# Revit family: pc-rp40160kal20_50hz
name_source: partatom
category: 機械設備
units: mm (PartAtom-declared; Revit-internal decimal feet)

## family parameters
OmniClass タイトル = Split System Air Conditioning Units
OmniClass 番号 = 23.75.10.24.21.27.27
パーツ タイプ = 標準
ロード時にボイドで切り取り = いいえ
丸型コネクタ寸法 = 直径を使用
作業面ベース = いいえ
共有 = いいえ
常に垂直 = はい
部屋計算ポイント = はい

## types (20) — shared parameters
Clearance Bottom = 1800  [stored 5.90551 ft]
Clearance Front = 1500  [stored 4.92126 ft]
Clearance Left = 270  [stored 0.885827 ft]
Clearance Right = 300  [stored 0.984252 ft]
Clearance Top = 1  [stored 0.00328084 ft]
Depth = 680  [stored 2.23097 ft]
Height = 236
Height_本体 = 230  [stored 0.754593 ft]
IfcExportAs = IfcUnitaryEquipmentType
IfcExportType = AIRCONDITIONINGUNIT
OmniClassCode = 23-33 17 13 11
URL = https://www.mitsubishielectric.co.jp
Uniclass2015Code = Pr_70_65_03_84
Uniclass2015Title = Split coil remote air cooled condensing units
Uniclass2015Version = Systems v1.9
ケーブルサイズ1 = 0 mm
サービススペース = はい
ドレン管径 = 20 mm
ドレン管径 (外径) = 26 mm
ドレン管高さ = 190  [stored 0.62336 ft]
パネルマテリアル = <カテゴリ別>
仕様書バージョン = Version1.0
企業コード = 108420
冷媒ガス管高さ = 126  [stored 0.413386 ft]
冷媒液管高さ = 126  [stored 0.413386 ft]
冷媒管径 = 100 mm
冷媒高低圧ガス管径 = 0 mm
分類コード = 5.0053E+13
加湿給水管径 = 0 mm
参照している仕様書等のバージョン = 公共建築物標準仕様書（機械設備工事編）平成31年度版
吊りボルト_H = 50  [stored 0.164042 ft]
吊り位置Y = 320  [stored 1.04987 ft]
周波数 = 50 Hz
呼称 = 室内機_天井吊(露出)形
始動方式 = 直入
形式 = 天井吊（露出）形
推奨ブレーカー容量 = 0 A
本体マテリアル = <カテゴリ別>
極数 = 1
法定耐用年数 = 6
点検口 = はい
発停方法 = 付属スイッチ
相 = 1
積算_科目 = 1 空気調和設備
符号 = ACP-CR
背面_ドレン管接続口 = 233  [stored 0.764436 ft]
製品出荷対象 = 国内
製造元 = 三菱電機株式会社
設置方法 = 天井吊形
設計冷房能力 = 0 kW
設計冷房能力_顕熱 = 0 kW
設計暖房能力 = 0.00 kW
説明 = 店舗・事務所用パッケージエアコン(Mr.SLIM) [本体] 天吊形室内機
負荷分類 = 3_ファン類
運転質量 = 0.00 kg
電圧 = 0 V
zero-valued in all types: Clearance Back, 価格, 有効加湿量, 点検口設置範囲, 電源_H

## per-type parameters (varying)
- 天吊_PC-RP45KAL20: MAX風量=780.0 m³/h; MID風量=660.0 m³/h; MID風量2=600.0 m³/h; MIN風量=540.0 m³/h; Width=960  [stored 3.14961 ft]; モデル=PC-RP45KAL20; 冷媒ガス管径=13 mm; 冷媒液管径=6 mm; 冷媒管径符号=Ac; 冷房能力=4 kW; 吊り位置X=917  [stored 3.00853 ft]; 暖房能力=4.50 kW; 消費電力=0.05 kW; 消費電力_冷房=0.05 kW; 消費電力_暖房=0.04 kW; 背面_ガス管接続口=203  [stored 0.66601 ft]; 背面_液管接続口=184  [stored 0.603675 ft]; 製品質量=24.00 kg; 質量=28.80 kg; 電動機出力_送風機=0.09 kW; 音響パワーレベル(dB)=55; 音響パワーレベル_中 (dB)=53; 音響パワーレベル_弱 (dB)=50; 音響パワーレベル_強 (dB)=55; 音響パワーレベル_静 (dB)=48; 風量=780.0 m³/h; 風量_中 (㎥/min)=11; 風量_弱 (㎥/min)=10; 風量_強 (㎥/min)=13; 風量_静 (㎥/min)=9
- 天吊_PC-RP56KAL20: MAX風量=780.0 m³/h; MID風量=720.0 m³/h; MID風量2=660.0 m³/h; MIN風量=600.0 m³/h; Width=960  [stored 3.14961 ft]; モデル=PC-RP56KAL20; 冷媒ガス管径=13 mm; 冷媒液管径=6 mm; 冷媒管径符号=Ac; 冷房能力=5 kW; 吊り位置X=917  [stored 3.00853 ft]; 暖房能力=5.60 kW; 消費電力=0.06 kW; 消費電力_冷房=0.06 kW; 消費電力_暖房=0.05 kW; 背面_ガス管接続口=203  [stored 0.66601 ft]; 背面_液管接続口=184  [stored 0.603675 ft]; 製品質量=25.00 kg; 質量=30.00 kg; 電動機出力_送風機=0.09 kW; 音響パワーレベル(dB)=55; 音響パワーレベル_中 (dB)=53; 音響パワーレベル_弱 (dB)=50; 音響パワーレベル_強 (dB)=55; 音響パワーレベル_静 (dB)=48; 風量=780.0 m³/h; 風量_中 (㎥/min)=12; 風量_弱 (㎥/min)=11; 風量_強 (㎥/min)=13; 風量_静 (㎥/min)=10
- 天吊_PC-RP71KAL20: MAX風量=1200.0 m³/h; MID風量=1080.0 m³/h; MID風量2=960.0 m³/h; MIN風量=780.0 m³/h; Width=1280  [stored 4.19948 ft]; モデル=PC-RP71KAL20; 冷媒ガス管径=16 mm; 冷媒液管径=10 mm; 冷媒管径符号=Bd; 冷房能力=6.3 kW; 吊り位置X=1237  [stored 4.0584 ft]; 暖房能力=7.10 kW; 消費電力=0.10 kW; 消費電力_冷房=0.10 kW; 消費電力_暖房=0.09 kW; 背面_ガス管接続口=200  [stored 0.656168 ft]; 背面_液管接続口=180  [stored 0.590551 ft]; 製品質量=32.00 kg; 質量=38.40 kg; 電動機出力_送風機=0.10 kW; 音響パワーレベル(dB)=57; 音響パワーレベル_中 (dB)=55; 音響パワーレベル_弱 (dB)=53; 音響パワーレベル_強 (dB)=57; 音響パワーレベル_静 (dB)=50; 風量=1200.0 m³/h; 風量_中 (㎥/min)=18; 風量_弱 (㎥/min)=16; 風量_強 (㎥/min)=20; 風量_静 (㎥/min)=13
- 天吊_PC-RP80KAL20: MAX風量=1200.0 m³/h; MID風量=1080.0 m³/h; MID風量2=960.0 m³/h; MIN風量=780.0 m³/h; Width=1280  [stored 4.19948 ft]; モデル=PC-RP80KAL20; 冷媒ガス管径=16 mm; 冷媒液管径=10 mm; 冷媒管径符号=Bd; 冷房能力=7.1 kW; 吊り位置X=1237  [stored 4.0584 ft]; 暖房能力=8.00 kW; 消費電力=0.10 kW; 消費電力_冷房=0.10 kW; 消費電力_暖房=0.09 kW; 背面_ガス管接続口=200  [stored 0.656168 ft]; 背面_液管接続口=180  [stored 0.590551 ft]; 製品質量=32.00 kg; 質量=38.40 kg; 電動機出力_送風機=0.10 kW; 音響パワーレベル(dB)=57; 音響パワーレベル_中 (dB)=55; 音響パワーレベル_弱 (dB)=53; 音響パワーレベル_強 (dB)=57; 音響パワーレベル_静 (dB)=50; 風量=1200.0 m³/h; 風量_中 (㎥/min)=18; 風量_弱 (㎥/min)=16; 風量_強 (㎥/min)=20; 風量_静 (㎥/min)=13
- 天吊_PC-RP112KAL20: MAX風量=1740.0 m³/h; MID風量=1560.0 m³/h; MID風量2=1320.0 m³/h; MIN風量=1200.0 m³/h; Width=1600  [stored 5.24934 ft]; モデル=PC-RP112KAL20; 冷媒ガス管径=16 mm; 冷媒液管径=10 mm; 冷媒管径符号=Bd; 冷房能力=10 kW; 吊り位置X=1557  [stored 5.10827 ft]; 暖房能力=11.20 kW; 消費電力=0.12 kW; 消費電力_冷房=0.12 kW; 消費電力_暖房=0.11 kW; 背面_ガス管接続口=200  [stored 0.656168 ft]; 背面_液管接続口=180  [stored 0.590551 ft]; 製品質量=38.00 kg; 質量=45.60 kg; 電動機出力_送風機=0.16 kW; 音響パワーレベル(dB)=62; 音響パワーレベル_中 (dB)=59; 音響パワーレベル_弱 (dB)=56; 音響パワーレベル_強 (dB)=62; 音響パワーレベル_静 (dB)=54; 風量=1740.0 m³/h; 風量_中 (㎥/min)=26; 風量_弱 (㎥/min)=22; 風量_強 (㎥/min)=29; 風量_静 (㎥/min)=20
- 天吊_PC-RP140KAL20: MAX風量=1860.0 m³/h; MID風量=1620.0 m³/h; MID風量2=1440.0 m³/h; MIN風量=1260.0 m³/h; Width=1600  [stored 5.24934 ft]; モデル=PC-RP140KAL20; 冷媒ガス管径=16 mm; 冷媒液管径=10 mm; 冷媒管径符号=Bd; 冷房能力=12.5 kW; 吊り位置X=1557  [stored 5.10827 ft]; 暖房能力=14.00 kW; 消費電力=0.14 kW; 消費電力_冷房=0.14 kW; 消費電力_暖房=0.13 kW; 背面_ガス管接続口=200  [stored 0.656168 ft]; 背面_液管接続口=180  [stored 0.590551 ft]; 製品リリース年月=0; 製品質量=38.00 kg; 質量=45.60 kg; 電動機出力_送風機=0.16 kW; 音響パワーレベル(dB)=63; 音響パワーレベル_中 (dB)=61; 音響パワーレベル_弱 (dB)=58; 音響パワーレベル_強 (dB)=63; 音響パワーレベル_静 (dB)=56; 風量=1860.0 m³/h; 風量_中 (㎥/min)=27; 風量_弱 (㎥/min)=24; 風量_強 (㎥/min)=31; 風量_静 (㎥/min)=21
- 天吊_PC-RP160KAL20: MAX風量=1980.0 m³/h; MID風量=1680.0 m³/h; MID風量2=1500.0 m³/h; MIN風量=1320.0 m³/h; Width=1600  [stored 5.24934 ft]; モデル=PC-RP160KAL20; 冷媒ガス管径=16 mm; 冷媒液管径=10 mm; 冷媒管径符号=Bd; 冷房能力=14 kW; 吊り位置X=1557  [stored 5.10827 ft]; 暖房能力=16.00 kW; 消費電力=0.17 kW; 消費電力_冷房=0.17 kW; 消費電力_暖房=0.16 kW; 背面_ガス管接続口=200  [stored 0.656168 ft]; 背面_液管接続口=180  [stored 0.590551 ft]; 製品質量=38.00 kg; 質量=45.60 kg; 電動機出力_送風機=0.16 kW; 音響パワーレベル(dB)=65; 音響パワーレベル_中 (dB)=62; 音響パワーレベル_弱 (dB)=60; 音響パワーレベル_強 (dB)=65; 音響パワーレベル_静 (dB)=58; 風量=1980.0 m³/h; 風量_中 (㎥/min)=28; 風量_弱 (㎥/min)=25; 風量_強 (㎥/min)=33; 風量_静 (㎥/min)=22
- 天吊_PC-RP63KAL20: MAX風量=1020.0 m³/h; MID風量=900.0 m³/h; MID風量2=840.0 m³/h; MIN風量=720.0 m³/h; Width=1280  [stored 4.19948 ft]; モデル=PC-RP63KAL20; 冷媒ガス管径=13 mm; 冷媒液管径=6 mm; 冷媒管径符号=Ac; 冷房能力=5.6 kW; 吊り位置X=1237  [stored 4.0584 ft]; 暖房能力=6.30 kW; 消費電力=0.07 kW; 消費電力_冷房=0.07 kW; 消費電力_暖房=0.06 kW; 背面_ガス管接続口=203  [stored 0.66601 ft]; 背面_液管接続口=184  [stored 0.603675 ft]; 製品質量=32.00 kg; 質量=38.40 kg; 電動機出力_送風機=0.10 kW; 音響パワーレベル(dB)=55; 音響パワーレベル_中 (dB)=53; 音響パワーレベル_弱 (dB)=51; 音響パワーレベル_強 (dB)=55; 音響パワーレベル_静 (dB)=49; 風量=1020.0 m³/h; 風量_中 (㎥/min)=15; 風量_弱 (㎥/min)=14; 風量_強 (㎥/min)=17; 風量_静 (㎥/min)=12
- 天吊_PC-RP40KAL20: MAX風量=780.0 m³/h; MID風量=660.0 m³/h; MID風量2=600.0 m³/h; MIN風量=540.0 m³/h; Width=960  [stored 3.14961 ft]; モデル=PC-RP40KAL20; 冷媒ガス管径=13 mm; 冷媒液管径=6 mm; 冷媒管径符号=Ac; 冷房能力=3.6 kW; 吊り位置X=917  [stored 3.00853 ft]; 暖房能力=4.00 kW; 消費電力=0.05 kW; 消費電力_冷房=0.05 kW; 消費電力_暖房=0.04 kW; 背面_ガス管接続口=203  [stored 0.66601 ft]; 背面_液管接続口=184  [stored 0.603675 ft]; 製品質量=24.00 kg; 質量=28.80 kg; 電動機出力_送風機=0.09 kW; 音響パワーレベル(dB)=55; 音響パワーレベル_中 (dB)=53; 音響パワーレベル_弱 (dB)=50; 音響パワーレベル_強 (dB)=55; 音響パワーレベル_静 (dB)=48; 風量=780.0 m³/h; 風量_中 (㎥/min)=11; 風量_弱 (㎥/min)=10; 風量_強 (㎥/min)=13; 風量_静 (㎥/min)=9
- 天吊_PC-RP50KAL20: MAX風量=780.0 m³/h; MID風量=720.0 m³/h; MID風量2=660.0 m³/h; MIN風量=600.0 m³/h; Width=960  [stored 3.14961 ft]; モデル=PC-RP50KAL20; 冷媒ガス管径=13 mm; 冷媒液管径=6 mm; 冷媒管径符号=Ac; 冷房能力=4.5 kW; 吊り位置X=917  [stored 3.00853 ft]; 暖房能力=5.00 kW; 消費電力=0.06 kW; 消費電力_冷房=0.06 kW; 消費電力_暖房=0.05 kW; 背面_ガス管接続口=203  [stored 0.66601 ft]; 背面_液管接続口=184  [stored 0.603675 ft]; 製品質量=25.00 kg; 質量=30.00 kg; 電動機出力_送風機=0.09 kW; 音響パワーレベル(dB)=55; 音響パワーレベル_中 (dB)=53; 音響パワーレベル_弱 (dB)=50; 音響パワーレベル_強 (dB)=55; 音響パワーレベル_静 (dB)=48; 風量=780.0 m³/h; 風量_中 (㎥/min)=12; 風量_弱 (㎥/min)=11; 風量_強 (㎥/min)=13; 風量_静 (㎥/min)=10
- 天吊_PC-RP112KA20: MAX風量=1740.0 m³/h; MID風量=1560.0 m³/h; MID風量2=1320.0 m³/h; MIN風量=1200.0 m³/h; Width=1600  [stored 5.24934 ft]; モデル=PC-RP112KA20; 冷媒ガス管径=16 mm; 冷媒液管径=10 mm; 冷媒管径符号=Bd; 冷房能力=10 kW; 吊り位置X=1557  [stored 5.10827 ft]; 暖房能力=11.20 kW; 消費電力=0.12 kW; 消費電力_冷房=0.12 kW; 消費電力_暖房=0.11 kW; 背面_ガス管接続口=200  [stored 0.656168 ft]; 背面_液管接続口=180  [stored 0.590551 ft]; 製品質量=38.00 kg; 質量=45.60 kg; 電動機出力_送風機=0.16 kW; 音響パワーレベル(dB)=62; 音響パワーレベル_中 (dB)=59; 音響パワーレベル_弱 (dB)=56; 音響パワーレベル_強 (dB)=62; 音響パワーレベル_静 (dB)=54; 風量=1740.0 m³/h; 風量_中 (㎥/min)=26; 風量_弱 (㎥/min)=22; 風量_強 (㎥/min)=29; 風量_静 (㎥/min)=20
- 天吊_PC-RP140KA20: MAX風量=1860.0 m³/h; MID風量=1620.0 m³/h; MID風量2=1440.0 m³/h; MIN風量=1260.0 m³/h; Width=1600  [stored 5.24934 ft]; モデル=PC-RP140KA20; 冷媒ガス管径=16 mm; 冷媒液管径=10 mm; 冷媒管径符号=Bd; 冷房能力=12.5 kW; 吊り位置X=1557  [stored 5.10827 ft]; 暖房能力=14.00 kW; 消費電力=0.14 kW; 消費電力_冷房=0.14 kW; 消費電力_暖房=0.13 kW; 背面_ガス管接続口=200  [stored 0.656168 ft]; 背面_液管接続口=180  [stored 0.590551 ft]; 製品質量=38.00 kg; 質量=45.60 kg; 電動機出力_送風機=0.16 kW; 音響パワーレベル(dB)=63; 音響パワーレベル_中 (dB)=61; 音響パワーレベル_弱 (dB)=58; 音響パワーレベル_強 (dB)=63; 音響パワーレベル_静 (dB)=56; 風量=1860.0 m³/h; 風量_中 (㎥/min)=27; 風量_弱 (㎥/min)=24; 風量_強 (㎥/min)=31; 風量_静 (㎥/min)=21
- 天吊_PC-RP160KA20: MAX風量=1980.0 m³/h; MID風量=1680.0 m³/h; MID風量2=1500.0 m³/h; MIN風量=1320.0 m³/h; Width=1600  [stored 5.24934 ft]; モデル=PC-RP160KA20; 冷媒ガス管径=16 mm; 冷媒液管径=10 mm; 冷媒管径符号=Bd; 冷房能力=14 kW; 吊り位置X=1557  [stored 5.10827 ft]; 暖房能力=16.00 kW; 消費電力=0.17 kW; 消費電力_冷房=0.17 kW; 消費電力_暖房=0.16 kW; 背面_ガス管接続口=200  [stored 0.656168 ft]; 背面_液管接続口=180  [stored 0.590551 ft]; 製品質量=38.00 kg; 質量=45.60 kg; 電動機出力_送風機=0.16 kW; 音響パワーレベル(dB)=65; 音響パワーレベル_中 (dB)=62; 音響パワーレベル_弱 (dB)=60; 音響パワーレベル_強 (dB)=65; 音響パワーレベル_静 (dB)=58; 風量=1980.0 m³/h; 風量_中 (㎥/min)=28; 風量_弱 (㎥/min)=25; 風量_強 (㎥/min)=33; 風量_静 (㎥/min)=22
- 天吊_PC-RP40KA20: MAX風量=780.0 m³/h; MID風量=660.0 m³/h; MID風量2=600.0 m³/h; MIN風量=540.0 m³/h; Width=960  [stored 3.14961 ft]; モデル=PC-RP40KA20; 冷媒ガス管径=13 mm; 冷媒液管径=6 mm; 冷媒管径符号=Ac; 冷房能力=3.6 kW; 吊り位置X=917  [stored 3.00853 ft]; 暖房能力=4.00 kW; 消費電力=0.05 kW; 消費電力_冷房=0.05 kW; 消費電力_暖房=0.04 kW; 背面_ガス管接続口=203  [stored 0.66601 ft]; 背面_液管接続口=184  [stored 0.603675 ft]; 製品質量=24.00 kg; 質量=28.80 kg; 電動機出力_送風機=0.09 kW; 音響パワーレベル(dB)=55; 音響パワーレベル_中 (dB)=53; 音響パワーレベル_弱 (dB)=50; 音響パワーレベル_強 (dB)=55; 音響パワーレベル_静 (dB)=48; 風量=780.0 m³/h; 風量_中 (㎥/min)=11; 風量_弱 (㎥/min)=10; 風量_強 (㎥/min)=13; 風量_静 (㎥/min)=9
- 天吊_PC-RP45KA20: MAX風量=780.0 m³/h; MID風量=660.0 m³/h; MID風量2=600.0 m³/h; MIN風量=540.0 m³/h; Width=960  [stored 3.14961 ft]; モデル=PC-RP45KA20; 冷媒ガス管径=13 mm; 冷媒液管径=6 mm; 冷媒管径符号=Ac; 冷房能力=4 kW; 吊り位置X=917  [stored 3.00853 ft]; 暖房能力=4.50 kW; 消費電力=0.05 kW; 消費電力_冷房=0.05 kW; 消費電力_暖房=0.04 kW; 背面_ガス管接続口=203  [stored 0.66601 ft]; 背面_液管接続口=184  [stored 0.603675 ft]; 製品質量=24.00 kg; 質量=28.80 kg; 電動機出力_送風機=0.09 kW; 音響パワーレベル(dB)=55; 音響パワーレベル_中 (dB)=53; 音響パワーレベル_弱 (dB)=50; 音響パワーレベル_強 (dB)=55; 音響パワーレベル_静 (dB)=48; 風量=780.0 m³/h; 風量_中 (㎥/min)=11; 風量_弱 (㎥/min)=10; 風量_強 (㎥/min)=13; 風量_静 (㎥/min)=9
- 天吊_PC-RP50KA20: MAX風量=780.0 m³/h; MID風量=720.0 m³/h; MID風量2=660.0 m³/h; MIN風量=600.0 m³/h; Width=960  [stored 3.14961 ft]; モデル=PC-RP50KA20; 冷媒ガス管径=13 mm; 冷媒液管径=6 mm; 冷媒管径符号=Ac; 冷房能力=4.5 kW; 吊り位置X=917  [stored 3.00853 ft]; 暖房能力=5.00 kW; 消費電力=0.06 kW; 消費電力_冷房=0.06 kW; 消費電力_暖房=0.05 kW; 背面_ガス管接続口=203  [stored 0.66601 ft]; 背面_液管接続口=184  [stored 0.603675 ft]; 製品質量=25.00 kg; 質量=30.00 kg; 電動機出力_送風機=0.09 kW; 音響パワーレベル(dB)=55; 音響パワーレベル_中 (dB)=53; 音響パワーレベル_弱 (dB)=50; 音響パワーレベル_強 (dB)=55; 音響パワーレベル_静 (dB)=48; 風量=780.0 m³/h; 風量_中 (㎥/min)=12; 風量_弱 (㎥/min)=11; 風量_強 (㎥/min)=13; 風量_静 (㎥/min)=10
- 天吊_PC-RP56KA20: MAX風量=780.0 m³/h; MID風量=720.0 m³/h; MID風量2=660.0 m³/h; MIN風量=600.0 m³/h; Width=960  [stored 3.14961 ft]; モデル=PC-RP56KA20; 冷媒ガス管径=13 mm; 冷媒液管径=6 mm; 冷媒管径符号=Ac; 冷房能力=5 kW; 吊り位置X=917  [stored 3.00853 ft]; 暖房能力=5.60 kW; 消費電力=0.06 kW; 消費電力_冷房=0.06 kW; 消費電力_暖房=0.05 kW; 背面_ガス管接続口=203  [stored 0.66601 ft]; 背面_液管接続口=184  [stored 0.603675 ft]; 製品質量=25.00 kg; 質量=30.00 kg; 電動機出力_送風機=0.09 kW; 音響パワーレベル(dB)=55; 音響パワーレベル_中 (dB)=53; 音響パワーレベル_弱 (dB)=50; 音響パワーレベル_強 (dB)=55; 音響パワーレベル_静 (dB)=48; 風量=780.0 m³/h; 風量_中 (㎥/min)=12; 風量_弱 (㎥/min)=11; 風量_強 (㎥/min)=13; 風量_静 (㎥/min)=10
- 天吊_PC-RP63KA20: MAX風量=1020.0 m³/h; MID風量=900.0 m³/h; MID風量2=840.0 m³/h; MIN風量=720.0 m³/h; Width=1280  [stored 4.19948 ft]; モデル=PC-RP63KA20; 冷媒ガス管径=13 mm; 冷媒液管径=6 mm; 冷媒管径符号=Ac; 冷房能力=5.6 kW; 吊り位置X=1237  [stored 4.0584 ft]; 暖房能力=6.30 kW; 消費電力=0.07 kW; 消費電力_冷房=0.07 kW; 消費電力_暖房=0.06 kW; 背面_ガス管接続口=203  [stored 0.66601 ft]; 背面_液管接続口=184  [stored 0.603675 ft]; 製品質量=32.00 kg; 質量=38.40 kg; 電動機出力_送風機=0.10 kW; 音響パワーレベル(dB)=55; 音響パワーレベル_中 (dB)=53; 音響パワーレベル_弱 (dB)=51; 音響パワーレベル_強 (dB)=55; 音響パワーレベル_静 (dB)=49; 風量=1020.0 m³/h; 風量_中 (㎥/min)=15; 風量_弱 (㎥/min)=14; 風量_強 (㎥/min)=17; 風量_静 (㎥/min)=12
- 天吊_PC-RP71KA20: MAX風量=1200.0 m³/h; MID風量=1080.0 m³/h; MID風量2=960.0 m³/h; MIN風量=780.0 m³/h; Width=1280  [stored 4.19948 ft]; モデル=PC-RP71KA20; 冷媒ガス管径=16 mm; 冷媒液管径=10 mm; 冷媒管径符号=Bd; 冷房能力=6.3 kW; 吊り位置X=1237  [stored 4.0584 ft]; 暖房能力=7.10 kW; 消費電力=0.10 kW; 消費電力_冷房=0.10 kW; 消費電力_暖房=0.09 kW; 背面_ガス管接続口=200  [stored 0.656168 ft]; 背面_液管接続口=180  [stored 0.590551 ft]; 製品質量=32.00 kg; 質量=38.40 kg; 電動機出力_送風機=0.10 kW; 音響パワーレベル(dB)=57; 音響パワーレベル_中 (dB)=55; 音響パワーレベル_弱 (dB)=53; 音響パワーレベル_強 (dB)=57; 音響パワーレベル_静 (dB)=50; 風量=1200.0 m³/h; 風量_中 (㎥/min)=18; 風量_弱 (㎥/min)=16; 風量_強 (㎥/min)=20; 風量_静 (㎥/min)=13
- 天吊_PC-RP80KA20: MAX風量=1200.0 m³/h; MID風量=1080.0 m³/h; MID風量2=960.0 m³/h; MIN風量=780.0 m³/h; Width=1280  [stored 4.19948 ft]; モデル=PC-RP80KA20; 冷媒ガス管径=16 mm; 冷媒液管径=10 mm; 冷媒管径符号=Bd; 冷房能力=7.1 kW; 吊り位置X=1237  [stored 4.0584 ft]; 暖房能力=8.00 kW; 消費電力=0.10 kW; 消費電力_冷房=0.10 kW; 消費電力_暖房=0.09 kW; 背面_ガス管接続口=200  [stored 0.656168 ft]; 背面_液管接続口=180  [stored 0.590551 ft]; 製品質量=32.00 kg; 質量=38.40 kg; 電動機出力_送風機=0.10 kW; 音響パワーレベル(dB)=57; 音響パワーレベル_中 (dB)=55; 音響パワーレベル_弱 (dB)=53; 音響パワーレベル_強 (dB)=57; 音響パワーレベル_静 (dB)=50; 風量=1200.0 m³/h; 風量_中 (㎥/min)=18; 風量_弱 (㎥/min)=16; 風量_強 (㎥/min)=20; 風量_静 (㎥/min)=13

note: [stored X ft] marks values corroborated as IEEE doubles in the binary element streams (Revit-internal decimal feet)

## geometry (parser evidence)
native form markers: Blend x4
no freeform markers — native parametric forms only
